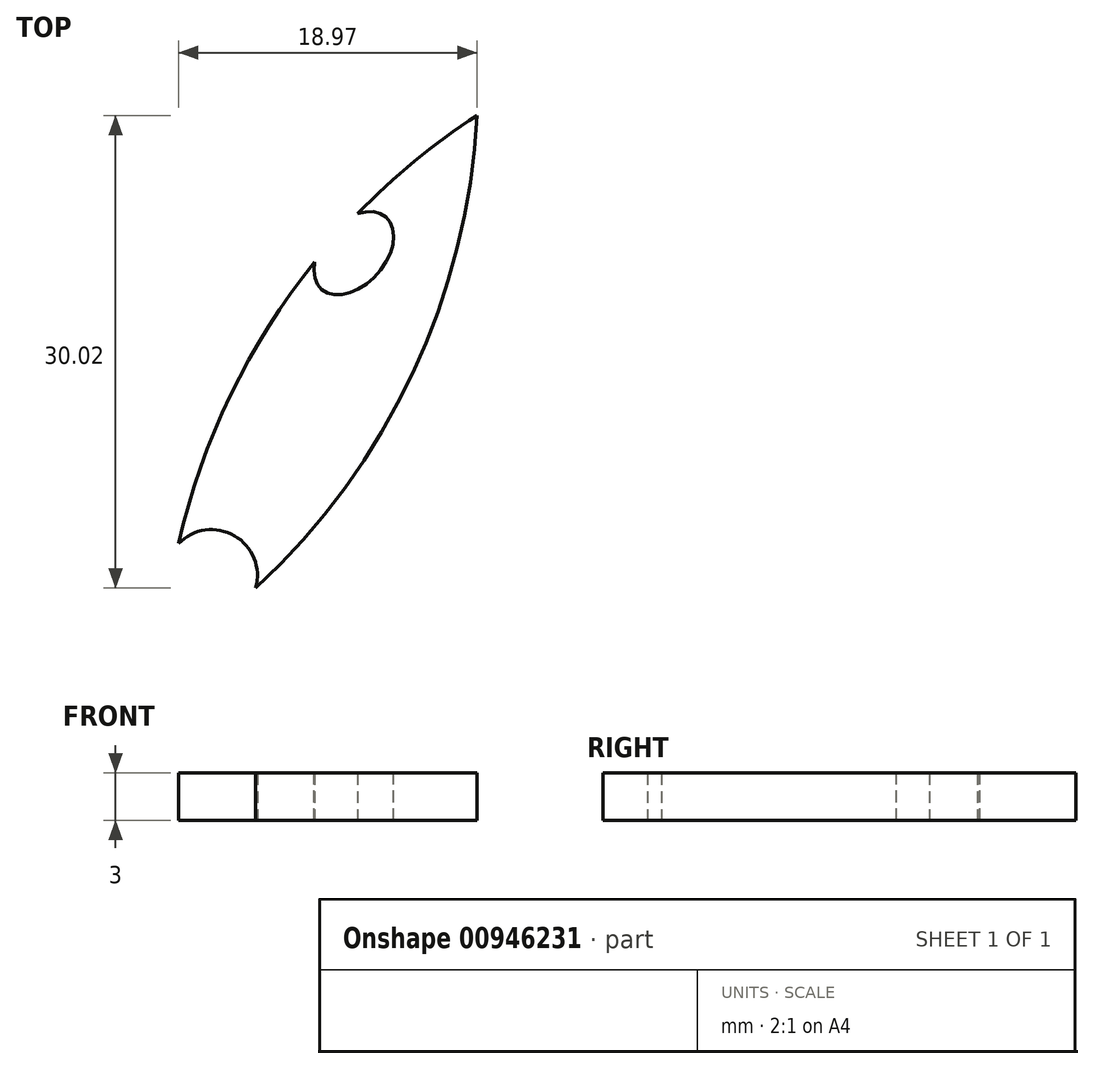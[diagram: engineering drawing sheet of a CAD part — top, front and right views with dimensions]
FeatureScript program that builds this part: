
annotation { "Feature Type Name" : "Feature", "Feature Type Description" : "" }
export const myFeature = defineFeature(function(context is Context, id is Id, definition is map)
    precondition{}
    {
        {
            var Q0;
            Q0=qCreatedBy(makeId("Top.planeOp"),FACE);
            var sketch = newSketch(context, id + "F0", { "sketchPlane" : qUnion([Q0])});
            skLineSegment(sketch, "E0", {"start": v(16, 11) * mm, "end": v(18.72, 12.97) * mm});
            skArc(sketch, "E1", {"start": v(14.24, 9.73) * mm, "mid": v(13.79, 11.36) * mm, "end": v(13.29, 12.97) * mm});
            skLineSegment(sketch, "E2", {"start": v(14.72, 7.81) * mm, "end": v(11.6, 7.81) * mm});
            skLineSegment(sketch, "E3", {"start": v(-19.81, 1) * mm, "end": v(-19.81, -0.63) * mm});
            skArc(sketch, "E4", {"start": v(-4, 30.02) * mm, "mid": v(-7.97, 27.12) * mm, "end": v(-11.6, 23.79) * mm});
            skArc(sketch, "E5", {"start": v(17.28, 7.81) * mm, "mid": v(16.52, 3.93) * mm, "end": v(16, 0) * mm});
            skArc(sketch, "E6", {"start": v(-25.42, -3.8) * mm, "mid": v(-25.25, -5.06) * mm, "end": v(-24.6, -6.14) * mm});
            skArc(sketch, "E7", {"start": v(-24.6, -6.14) * mm, "mid": v(-23.53, -5.97) * mm, "end": v(-22.59, -5.44) * mm});
            skLineSegment(sketch, "E8", {"start": v(-34.64, 20) * mm, "end": v(-34.64, -20) * mm});
            skLineSegment(sketch, "E9", {"start": v(34.64, -20) * mm, "end": v(0, -40) * mm});
            skLineSegment(sketch, "E10", {"start": v(34.64, -20) * mm, "end": v(34.64, 20) * mm});
            skLineSegment(sketch, "E11", {"start": v(-21.22, 1.82) * mm, "end": v(-19.81, 1) * mm});
            skArc(sketch, "E12", {"start": v(-14.32, 20.71) * mm, "mid": v(-19.66, 12.26) * mm, "end": v(-22.97, 2.83) * mm});
            skArc(sketch, "E13", {"start": v(-22.64, 1) * mm, "mid": v(-23.73, -1.7) * mm, "end": v(-24, -4.62) * mm});
            skArc(sketch, "E14", {"start": v(-24, -4.62) * mm, "mid": v(-21.62, -2.92) * mm, "end": v(-19.81, -0.63) * mm});
            skArc(sketch, "E15", {"start": v(-3.65, -30.29) * mm, "mid": v(-1.58, -30.2) * mm, "end": v(0.38, -29.55) * mm});
            skLineSegment(sketch, "E16", {"start": v(-22.64, 1) * mm, "end": v(-21.22, 1.82) * mm});
            skLineSegment(sketch, "E17", {"start": v(17.76, 9.73) * mm, "end": v(20.4, 7.81) * mm});
            skEllipticalArc(sketch, "E18", {});
            skArc(sketch, "E19", {"start": v(8, -12.94) * mm, "mid": v(7.73, -9.28) * mm, "end": v(6.93, -5.69) * mm});
            skLineSegment(sketch, "E20", {"start": v(-34.64, -20) * mm, "end": v(0, -40) * mm});
            skEllipticalArc(sketch, "E21", {});
            skArc(sketch, "E22", {"start": v(-18.07, 0) * mm, "mid": v(-19.41, 3.33) * mm, "end": v(-22.97, 2.83) * mm});
            skEllipticalArc(sketch, "E23", {});
            skArc(sketch, "E24", {"start": v(-18.07, 0) * mm, "mid": v(-8.1, 13.64) * mm, "end": v(-4, 30.02) * mm});
            skEllipticalArc(sketch, "E25", {});
            skLineSegment(sketch, "E26", {"start": v(0, 40) * mm, "end": v(-34.64, 20) * mm});
            skLineSegment(sketch, "E27", {"start": v(34.64, 20) * mm, "end": v(0, 40) * mm});
            skCircle(sketch, "E28", {"center": v(0, -23.1) * mm, "radius": 4.62 * mm});
            skArc(sketch, "E29", {"start": v(9.07, -5.69) * mm, "mid": v(8.27, -9.28) * mm, "end": v(8, -12.94) * mm});
            skLineSegment(sketch, "E30", {"start": v(9.07, -5.69) * mm, "end": v(11.54, -4.62) * mm});
            skLineSegment(sketch, "E31", {"start": v(9.07, -3.55) * mm, "end": v(11.54, -4.62) * mm});
            skLineSegment(sketch, "E32", {"start": v(9.07, -3.55) * mm, "end": v(8, -1.08) * mm});
            skLineSegment(sketch, "E33", {"start": v(6.93, -3.55) * mm, "end": v(8, -1.08) * mm});
            skLineSegment(sketch, "E34", {"start": v(6.93, -3.55) * mm, "end": v(4.46, -4.62) * mm});
            skLineSegment(sketch, "E35", {"start": v(6.93, -5.69) * mm, "end": v(4.46, -4.62) * mm});
            skArc(sketch, "E36", {"start": v(21.07, -12.62) * mm, "mid": v(20.27, -16.2) * mm, "end": v(20, -19.87) * mm});
            skArc(sketch, "E37", {"start": v(20, -19.87) * mm, "mid": v(19.73, -16.2) * mm, "end": v(18.93, -12.62) * mm});
            skLineSegment(sketch, "E38", {"start": v(18.93, -12.62) * mm, "end": v(16.46, -11.55) * mm});
            skLineSegment(sketch, "E39", {"start": v(18.93, -10.48) * mm, "end": v(16.46, -11.55) * mm});
            skLineSegment(sketch, "E40", {"start": v(18.93, -10.48) * mm, "end": v(20, -8) * mm});
            skLineSegment(sketch, "E41", {"start": v(21.07, -10.48) * mm, "end": v(20, -8) * mm});
            skLineSegment(sketch, "E42", {"start": v(21.07, -10.48) * mm, "end": v(23.54, -11.55) * mm});
            skLineSegment(sketch, "E43", {"start": v(21.07, -12.62) * mm, "end": v(23.54, -11.55) * mm});
            skLineSegment(sketch, "E44", {"start": v(11.6, 7.81) * mm, "end": v(14.24, 9.73) * mm});
            skLineSegment(sketch, "E45", {"start": v(13.29, 12.97) * mm, "end": v(16, 11) * mm});
            skArc(sketch, "E46", {"start": v(16, 0) * mm, "mid": v(15.49, 3.93) * mm, "end": v(14.72, 7.81) * mm});
            skArc(sketch, "E47", {"start": v(18.72, 12.97) * mm, "mid": v(18.21, 11.36) * mm, "end": v(17.76, 9.73) * mm});
            skLineSegment(sketch, "E48", {"start": v(20.4, 7.81) * mm, "end": v(17.28, 7.81) * mm});
            skLineSegment(sketch, "E49", {"start": v(9.07, -5.69) * mm, "end": v(6.93, -3.55) * mm, "construction": true});
            skPoint(sketch, "E50", {"position": v(8, -4.62) * mm});
            const initialGuessF0  = {"E18": [-0.011835856342462906, 0.021274626263381315, 0.6671519867218451, 0.7449216244767601, 0.003066820782988711, 0.001997104924167824, 2.313906, 0.845184692820414], "E21": [-0.00428764486884414, -0.012970038006298498, 0.9624687095500947, -0.27139267332957884, 0.02321225604516635, 0.01694522537442038, 2.958237, 4.943352], "E23": [-0.00614458734444925, -0.014928535768250874, -0.8660254053109743, 0.49999999735596273, 0.018985638312373057, 0.012858117091493412, 2.232337, 2.321935], "E25": [-0.00614458734444925, -0.014928535768250874, -0.8660254053109743, 0.49999999735596273, 0.018985638312373057, 0.012858117091493412, 0, 2.232337]};
            skSetInitialGuess(sketch, initialGuessF0);
            skSolve(sketch);
        }
        {
            var Q0;
            Q0=qCreatedBy(makeId("Top.planeOp"),FACE);
            var sketch = newSketch(context, id + "F1", { "sketchPlane" : qUnion([Q0])});
            skLineSegment(sketch, "E51.0", {"start": v(34.64, 20) * mm, "end": v(25.98, 25) * mm, "construction": true});
            skLineSegment(sketch, "E52.0", {"start": v(34.64, -20) * mm, "end": v(34.64, 20) * mm, "construction": true});
            skLineSegment(sketch, "E53.0.0", {"start": v(5.6, 3.36) * mm, "end": v(7.19, 2.67) * mm});
            skArc(sketch, "E53.0.1", {"start": v(7.19, 2.67) * mm, "mid": v(7.62, 0.82) * mm, "end": v(7.88, -1.07) * mm});
            skArc(sketch, "E53.0.2", {"start": v(7.88, -1.07) * mm, "mid": v(8.13, 0.82) * mm, "end": v(8.57, 2.67) * mm});
            skLineSegment(sketch, "E53.0.3", {"start": v(8.57, 2.67) * mm, "end": v(10.16, 3.36) * mm});
            skLineSegment(sketch, "E53.0.4", {"start": v(10.16, 3.36) * mm, "end": v(8.57, 4.05) * mm});
            skLineSegment(sketch, "E53.0.5", {"start": v(8.57, 4.05) * mm, "end": v(7.88, 5.64) * mm});
            skLineSegment(sketch, "E53.0.6", {"start": v(7.88, 5.64) * mm, "end": v(7.19, 4.05) * mm});
            skLineSegment(sketch, "E53.0.7", {"start": v(7.19, 4.05) * mm, "end": v(5.6, 3.36) * mm});
            skLineSegment(sketch, "E54.0.0", {"start": v(17.6, -3.57) * mm, "end": v(19.19, -4.26) * mm});
            skArc(sketch, "E54.0.1", {"start": v(19.19, -4.26) * mm, "mid": v(19.62, -6.11) * mm, "end": v(19.88, -8) * mm});
            skArc(sketch, "E54.0.2", {"start": v(19.88, -8) * mm, "mid": v(20.13, -6.11) * mm, "end": v(20.57, -4.26) * mm});
            skLineSegment(sketch, "E54.0.3", {"start": v(20.57, -4.26) * mm, "end": v(22.16, -3.57) * mm});
            skLineSegment(sketch, "E54.0.4", {"start": v(22.16, -3.57) * mm, "end": v(20.57, -2.88) * mm});
            skLineSegment(sketch, "E54.0.5", {"start": v(20.57, -2.88) * mm, "end": v(19.88, -1.29) * mm});
            skLineSegment(sketch, "E54.0.6", {"start": v(19.88, -1.29) * mm, "end": v(19.19, -2.88) * mm});
            skLineSegment(sketch, "E54.0.7", {"start": v(19.19, -2.88) * mm, "end": v(17.6, -3.57) * mm});
            skArc(sketch, "E55.0.0", {"start": v(17.06, 17.5) * mm, "mid": v(17.36, 18.58) * mm, "end": v(17.67, 19.66) * mm});
            skLineSegment(sketch, "E55.0.1", {"start": v(17.67, 19.66) * mm, "end": v(15.88, 18.36) * mm});
            skLineSegment(sketch, "E55.0.2", {"start": v(15.88, 18.36) * mm, "end": v(14.09, 19.66) * mm});
            skArc(sketch, "E55.0.3", {"start": v(14.09, 19.66) * mm, "mid": v(14.4, 18.58) * mm, "end": v(14.7, 17.5) * mm});
            skLineSegment(sketch, "E55.0.4", {"start": v(14.7, 17.5) * mm, "end": v(13.02, 16.29) * mm});
            skLineSegment(sketch, "E55.0.5", {"start": v(13.02, 16.29) * mm, "end": v(15, 16.29) * mm});
            skArc(sketch, "E55.0.6", {"start": v(15, 16.29) * mm, "mid": v(15.47, 14.08) * mm, "end": v(15.88, 11.85) * mm});
            skArc(sketch, "E55.0.7", {"start": v(15.88, 11.85) * mm, "mid": v(16.28, 14.08) * mm, "end": v(16.76, 16.29) * mm});
            skLineSegment(sketch, "E55.0.8", {"start": v(16.76, 16.29) * mm, "end": v(18.73, 16.29) * mm});
            skLineSegment(sketch, "E55.0.9", {"start": v(18.73, 16.29) * mm, "end": v(17.06, 17.5) * mm});
            skLineSegment(sketch, "E56", {"start": v(14.7, 17.5) * mm, "end": v(17.06, 17.5) * mm, "construction": true});
            skPoint(sketch, "E57", {"position": v(15.88, 17.5) * mm});
            skLineSegment(sketch, "E58", {"start": v(34.64, -20) * mm, "end": v(0, 40) * mm, "construction": true});
            skLineSegment(sketch, "E59", {"start": v(17.32, 30) * mm, "end": v(11.55, 20) * mm, "construction": true});
            skLineSegment(sketch, "E60", {"start": v(17.32, 30) * mm, "end": v(0, 40) * mm, "construction": true});
            skLineSegment(sketch, "E61", {"start": v(25.98, 25) * mm, "end": v(17.32, 30) * mm, "construction": true});
            skLineSegment(sketch, "E62", {"start": v(25.98, 25) * mm, "end": v(17.32, 10) * mm, "construction": true});
            skLineSegment(sketch, "E63", {"start": v(11.55, 20) * mm, "end": v(23.1, 20) * mm, "construction": true});
            skLineSegment(sketch, "E64", {"start": v(23.1, 20) * mm, "end": v(17.32, 10) * mm, "construction": true});
            skLineSegment(sketch, "E65", {"start": v(11.55, 20) * mm, "end": v(20.2, 15) * mm, "construction": true});
            skSolve(sketch);
        }
        {
            var Q0;
            Q0=qCreatedBy(makeId("Top.planeOp"),FACE);
            var sketch = newSketch(context, id + "F2", { "sketchPlane" : qUnion([Q0])});
            skArc(sketch, "E66.0.0", {"start": v(-22.97, 2.83) * mm, "mid": v(-19.41, 3.33) * mm, "end": v(-18.07, 0) * mm});
            skArc(sketch, "E66.0.1", {"start": v(-18.07, 0) * mm, "mid": v(-8.1, 13.64) * mm, "end": v(-4, 30.02) * mm});
            skArc(sketch, "E66.0.2", {"start": v(-4, 30.02) * mm, "mid": v(-7.97, 27.12) * mm, "end": v(-11.6, 23.79) * mm});
            skEllipticalArc(sketch, "E66.0.3", {});
            skArc(sketch, "E66.0.4", {"start": v(-14.32, 20.71) * mm, "mid": v(-19.66, 12.26) * mm, "end": v(-22.97, 2.83) * mm});
            skLineSegment(sketch, "E67.0.0", {"start": v(-21.22, 1.82) * mm, "end": v(-22.64, 1) * mm});
            skArc(sketch, "E67.0.1", {"start": v(-22.64, 1) * mm, "mid": v(-23.73, -1.7) * mm, "end": v(-24, -4.62) * mm});
            skArc(sketch, "E67.0.2", {"start": v(-24, -4.62) * mm, "mid": v(-21.62, -2.92) * mm, "end": v(-19.81, -0.63) * mm});
            skLineSegment(sketch, "E67.0.3", {"start": v(-19.81, -0.63) * mm, "end": v(-19.81, 1) * mm});
            skLineSegment(sketch, "E67.0.4", {"start": v(-19.81, 1) * mm, "end": v(-21.22, 1.82) * mm});
            skEllipticalArc(sketch, "E68.0.0", {});
            skEllipticalArc(sketch, "E68.0.1", {});
            skArc(sketch, "E68.0.2", {"start": v(-22.59, -5.44) * mm, "mid": v(-23.53, -5.97) * mm, "end": v(-24.6, -6.14) * mm});
            skArc(sketch, "E68.0.3", {"start": v(-24.6, -6.14) * mm, "mid": v(-25.25, -5.06) * mm, "end": v(-25.42, -3.8) * mm});
            skEllipticalArc(sketch, "E68.0.4", {});
            skArc(sketch, "E68.0.5", {"start": v(-3.65, -30.29) * mm, "mid": v(-1.58, -30.2) * mm, "end": v(0.38, -29.55) * mm});
            skCircle(sketch, "E69.0.0", {"center": v(0, -23.1) * mm, "radius": 4.62 * mm});
            skLineSegment(sketch, "E70.0", {"start": v(-34.64, 20) * mm, "end": v(-34.64, -20) * mm});
            skLineSegment(sketch, "E71.0", {"start": v(0, 40) * mm, "end": v(-34.64, 20) * mm});
            skLineSegment(sketch, "E72.0", {"start": v(34.64, 20) * mm, "end": v(0, 40) * mm});
            skLineSegment(sketch, "E73.0", {"start": v(34.64, -20) * mm, "end": v(34.64, 20) * mm});
            skLineSegment(sketch, "E74.0", {"start": v(34.64, -20) * mm, "end": v(0, -40) * mm});
            skLineSegment(sketch, "E75.0", {"start": v(-34.64, -20) * mm, "end": v(0, -40) * mm});
            skLineSegment(sketch, "E76.0.0", {"start": v(19.88, -1.29) * mm, "end": v(19.19, -2.88) * mm});
            skLineSegment(sketch, "E76.0.1", {"start": v(19.19, -2.88) * mm, "end": v(17.6, -3.57) * mm});
            skLineSegment(sketch, "E76.0.2", {"start": v(17.6, -3.57) * mm, "end": v(19.19, -4.26) * mm});
            skArc(sketch, "E76.0.3", {"start": v(19.19, -4.26) * mm, "mid": v(19.62, -6.11) * mm, "end": v(19.88, -8) * mm});
            skArc(sketch, "E76.0.4", {"start": v(19.88, -8) * mm, "mid": v(20.13, -6.11) * mm, "end": v(20.57, -4.26) * mm});
            skLineSegment(sketch, "E76.0.5", {"start": v(20.57, -4.26) * mm, "end": v(22.16, -3.57) * mm});
            skLineSegment(sketch, "E76.0.6", {"start": v(22.16, -3.57) * mm, "end": v(20.57, -2.88) * mm});
            skLineSegment(sketch, "E76.0.7", {"start": v(20.57, -2.88) * mm, "end": v(19.88, -1.29) * mm});
            skLineSegment(sketch, "E77.0.0", {"start": v(7.88, 5.64) * mm, "end": v(7.19, 4.05) * mm});
            skLineSegment(sketch, "E77.0.1", {"start": v(7.19, 4.05) * mm, "end": v(5.6, 3.36) * mm});
            skLineSegment(sketch, "E77.0.2", {"start": v(5.6, 3.36) * mm, "end": v(7.19, 2.67) * mm});
            skArc(sketch, "E77.0.3", {"start": v(7.19, 2.67) * mm, "mid": v(7.62, 0.82) * mm, "end": v(7.88, -1.07) * mm});
            skArc(sketch, "E77.0.4", {"start": v(7.88, -1.07) * mm, "mid": v(8.13, 0.82) * mm, "end": v(8.57, 2.67) * mm});
            skLineSegment(sketch, "E77.0.5", {"start": v(8.57, 2.67) * mm, "end": v(10.16, 3.36) * mm});
            skLineSegment(sketch, "E77.0.6", {"start": v(10.16, 3.36) * mm, "end": v(8.57, 4.05) * mm});
            skLineSegment(sketch, "E77.0.7", {"start": v(8.57, 4.05) * mm, "end": v(7.88, 5.64) * mm});
            skLineSegment(sketch, "E78.0.0", {"start": v(16.76, 16.29) * mm, "end": v(18.73, 16.29) * mm});
            skLineSegment(sketch, "E78.0.1", {"start": v(18.73, 16.29) * mm, "end": v(17.06, 17.5) * mm});
            skArc(sketch, "E78.0.2", {"start": v(17.06, 17.5) * mm, "mid": v(17.36, 18.58) * mm, "end": v(17.67, 19.66) * mm});
            skLineSegment(sketch, "E78.0.3", {"start": v(17.67, 19.66) * mm, "end": v(15.88, 18.36) * mm});
            skLineSegment(sketch, "E78.0.4", {"start": v(15.88, 18.36) * mm, "end": v(14.09, 19.66) * mm});
            skArc(sketch, "E78.0.5", {"start": v(14.09, 19.66) * mm, "mid": v(14.4, 18.58) * mm, "end": v(14.7, 17.5) * mm});
            skLineSegment(sketch, "E78.0.6", {"start": v(14.7, 17.5) * mm, "end": v(13.02, 16.29) * mm});
            skLineSegment(sketch, "E78.0.7", {"start": v(13.02, 16.29) * mm, "end": v(15, 16.29) * mm});
            skArc(sketch, "E78.0.8", {"start": v(15, 16.29) * mm, "mid": v(15.47, 14.08) * mm, "end": v(15.88, 11.85) * mm});
            skArc(sketch, "E78.0.9", {"start": v(15.88, 11.85) * mm, "mid": v(16.28, 14.08) * mm, "end": v(16.76, 16.29) * mm});
            const initialGuessF2  = {"E66.0.3": [-0.011835856342462906, 0.021274626263381315, 0.6671519867218451, 0.7449216244767601, 0.003066820782988711, 0.001997104924167824, 2.313906, 0.8451845801532278], "E68.0.0": [-0.00614458734444925, -0.014928535768250874, -0.8660254053109743, 0.49999999735596273, 0.018985638312373057, 0.012858117091493412, 2.232337, 2.321935037686714], "E68.0.1": [-0.00614458734444925, -0.014928535768250874, -0.8660254053109743, 0.49999999735596273, 0.018985638312373057, 0.012858117091493412, 0, 2.232337], "E68.0.4": [-0.00428764486884414, -0.012970038006298498, 0.9624687095500947, -0.27139267332957884, 0.02321225604516635, 0.01694522537442038, 2.958237, 4.943352]};
            skSetInitialGuess(sketch, initialGuessF2);
            skSolve(sketch);
        }
        {
            var Q0;
            Q0=makeQuery(id+"F2.imprint","IMPRINT",FACE,{"disambiguationData":[TD([[makeQuery(id+"F2.imprint","IMPRINT",EDGE,{"derivedFrom":sQuery(id+"F2.wireOp",EDGE,"E66.0.0")}),-1.0]])]});
            extrude(context, id + "F3", {"entities" : qUnion([Q0]), "depth" : 3 * mm, "offsetDistance" : 25 * mm});
        }
    });
